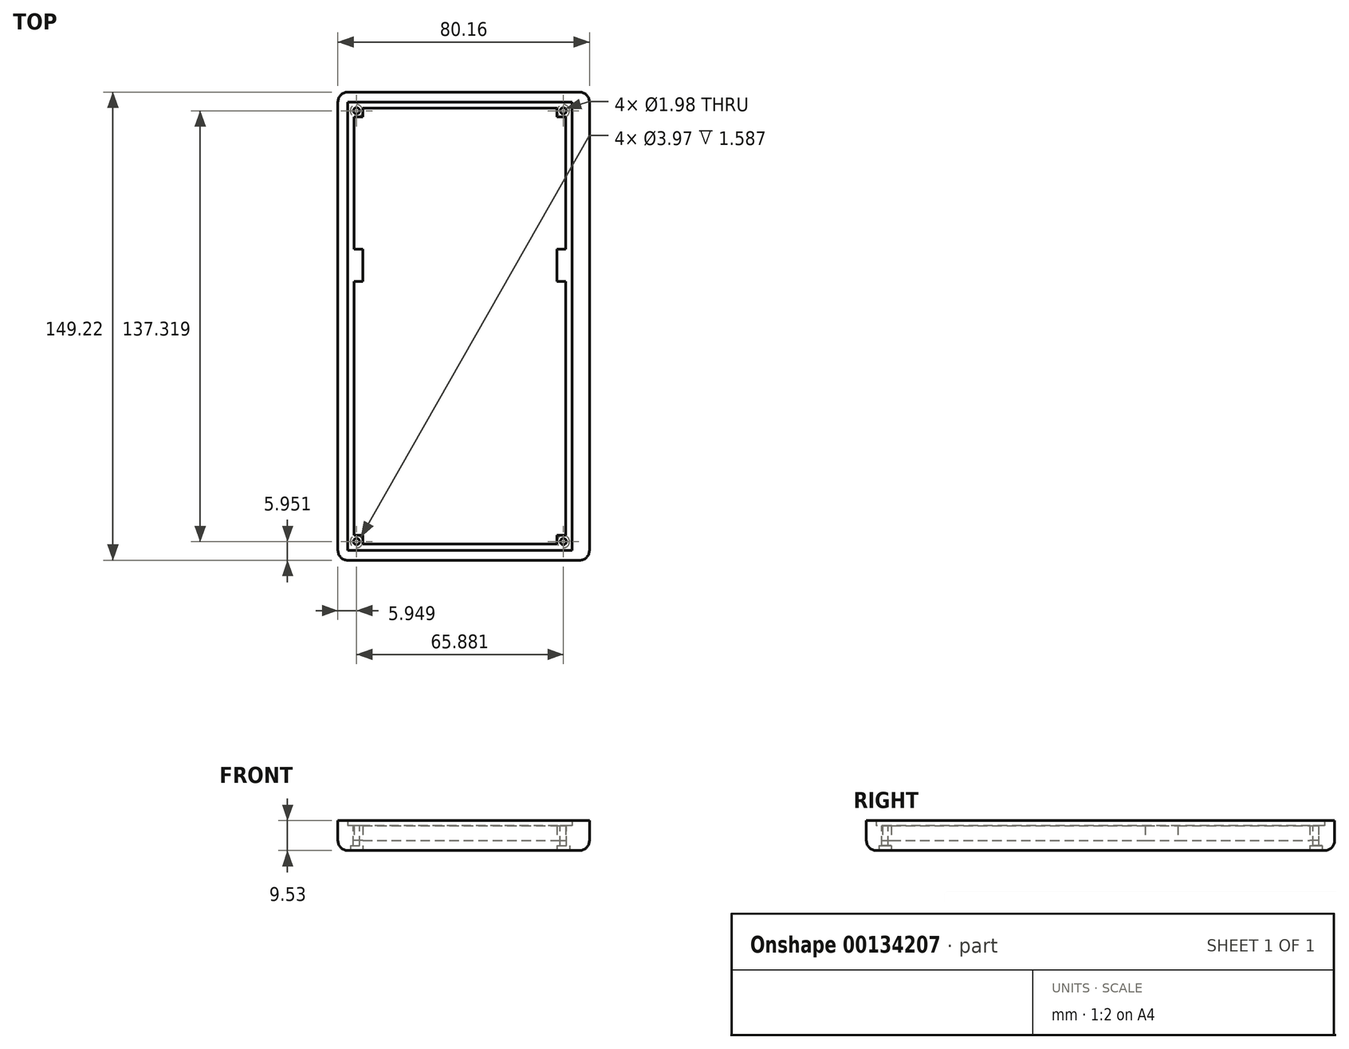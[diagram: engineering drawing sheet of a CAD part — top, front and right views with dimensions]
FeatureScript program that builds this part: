
annotation { "Feature Type Name" : "Feature", "Feature Type Description" : "" }
export const myFeature = defineFeature(function(context is Context, id is Id, definition is map)
    precondition{}
    {
        {
            var Q0;
            Q0=qCreatedBy(makeId("Top.planeOp"),FACE);
            var sketch = newSketch(context, id + "F0", { "sketchPlane" : qUnion([Q0])});
            skLineSegment(sketch, "E0.right", {"start": v(-36.9, -71.44) * mm, "end": v(-36.9, 71.44) * mm});
            skPoint(sketch, "E0.middle", {"position": v(0, 0) * mm});
            skLineSegment(sketch, "E1", {"start": v(-40.08, 0) * mm, "end": v(-40.08, -71.44) * mm});
            skLineSegment(sketch, "E2", {"start": v(-36.9, -74.61) * mm, "end": v(36.9, -74.61) * mm});
            skLineSegment(sketch, "E3", {"start": v(40.08, -71.44) * mm, "end": v(40.08, 71.44) * mm});
            skLineSegment(sketch, "E4", {"start": v(36.9, 74.61) * mm, "end": v(-36.9, 74.61) * mm});
            skLineSegment(sketch, "E5", {"start": v(-40.08, 71.44) * mm, "end": v(-40.08, 0) * mm});
            skPoint(sketch, "E6.visualSharp", {"position": v(-40.08, 74.61) * mm});
            skArc(sketch, "E6.filletArc", {"start": v(-36.9, 74.61) * mm, "mid": v(-39.15, 73.68) * mm, "end": v(-40.08, 71.44) * mm});
            skPoint(sketch, "E7.visualSharp", {"position": v(40.08, 74.61) * mm});
            skArc(sketch, "E7.filletArc", {"start": v(40.08, 71.44) * mm, "mid": v(39.15, 73.68) * mm, "end": v(36.9, 74.61) * mm});
            skPoint(sketch, "E8.visualSharp", {"position": v(40.08, -74.61) * mm});
            skArc(sketch, "E8.filletArc", {"start": v(36.9, -74.61) * mm, "mid": v(39.15, -73.68) * mm, "end": v(40.08, -71.44) * mm});
            skPoint(sketch, "E9.visualSharp", {"position": v(-40.08, -74.61) * mm});
            skArc(sketch, "E9.filletArc", {"start": v(-40.08, -71.44) * mm, "mid": v(-39.15, -73.68) * mm, "end": v(-36.9, -74.61) * mm});
            skLineSegment(sketch, "E10", {"start": v(34.53, 71.44) * mm, "end": v(34.53, -71.44) * mm});
            skLineSegment(sketch, "E11", {"start": v(-36.9, 71.44) * mm, "end": v(34.53, 71.44) * mm});
            skLineSegment(sketch, "E12", {"start": v(-36.9, -71.44) * mm, "end": v(34.53, -71.44) * mm});
            skSolve(sketch);
        }
        {
            var Q0;
            Q0=makeQuery(id+"F0.imprint","IMPRINT",FACE,{"disambiguationData":[TD([[makeQuery(id+"F0.imprint","IMPRINT",EDGE,{"derivedFrom":sQuery(id+"F0.wireOp",EDGE,"E0.right")}),1.0]])]});
            extrude(context, id + "F1", {"entities" : qUnion([Q0]), "depth" : 6.35 * mm});
        }
        {
            var Q0;
            Q0=makeQuery(id+"F1.opExtrude","CAP_FACE",FACE,{"disambiguationData":[OSD([sQuery(id+"F0.wireOp",EDGE,"E0.right"),sQuery(id+"F0.wireOp",EDGE,"E1"),sQuery(id+"F0.wireOp",EDGE,"E2"),sQuery(id+"F0.wireOp",EDGE,"E3"),sQuery(id+"F0.wireOp",EDGE,"E4"),sQuery(id+"F0.wireOp",EDGE,"E5"),sQuery(id+"F0.wireOp",EDGE,"E6.filletArc"),sQuery(id+"F0.wireOp",EDGE,"E7.filletArc"),sQuery(id+"F0.wireOp",EDGE,"E8.filletArc"),sQuery(id+"F0.wireOp",EDGE,"E9.filletArc"),sQuery(id+"F0.wireOp",EDGE,"E10"),sQuery(id+"F0.wireOp",EDGE,"E11"),sQuery(id+"F0.wireOp",EDGE,"E12")])],"isStart":true});
            var sketch = newSketch(context, id + "F2", { "sketchPlane" : qUnion([Q0])});
            skLineSegment(sketch, "E13.0", {"start": v(-40.08, -71.44) * mm, "end": v(-40.08, 71.44) * mm});
            skLineSegment(sketch, "E14.0", {"start": v(-36.9, 71.44) * mm, "end": v(-36.9, -71.44) * mm});
            skLineSegment(sketch, "E15.0", {"start": v(-36.9, 71.44) * mm, "end": v(34.53, 71.44) * mm});
            skLineSegment(sketch, "E16.0", {"start": v(34.53, -71.44) * mm, "end": v(34.53, 71.44) * mm});
            skLineSegment(sketch, "E17.0", {"start": v(-36.9, -71.44) * mm, "end": v(34.53, -71.44) * mm});
            skLineSegment(sketch, "E18.0.0", {"start": v(-40.08, 71.44) * mm, "end": v(-40.08, -71.44) * mm});
            skArc(sketch, "E18.0.1", {"start": v(-40.08, -71.44) * mm, "mid": v(-39.15, -73.68) * mm, "end": v(-36.9, -74.61) * mm});
            skLineSegment(sketch, "E18.0.2", {"start": v(-36.9, -74.61) * mm, "end": v(36.9, -74.61) * mm});
            skArc(sketch, "E18.0.3", {"start": v(36.9, -74.61) * mm, "mid": v(39.15, -73.68) * mm, "end": v(40.08, -71.44) * mm});
            skLineSegment(sketch, "E18.0.4", {"start": v(40.08, -71.44) * mm, "end": v(40.08, 71.44) * mm});
            skArc(sketch, "E18.0.5", {"start": v(40.08, 71.44) * mm, "mid": v(39.15, 73.68) * mm, "end": v(36.9, 74.61) * mm});
            skLineSegment(sketch, "E18.0.6", {"start": v(36.9, 74.61) * mm, "end": v(-36.9, 74.61) * mm});
            skArc(sketch, "E18.0.7", {"start": v(-36.9, 74.61) * mm, "mid": v(-39.15, 73.68) * mm, "end": v(-40.08, 71.44) * mm});
            skLineSegment(sketch, "E19.bottom", {"start": v(-32.15, 69.45) * mm, "end": v(29.77, 69.45) * mm});
            skLineSegment(sketch, "E19.top", {"start": v(-32.15, -69.45) * mm, "end": v(29.77, -69.45) * mm});
            skLineSegment(sketch, "E19.left", {"start": v(-34.92, 66.68) * mm, "end": v(-34.92, 24.6) * mm});
            skLineSegment(sketch, "E19.right", {"start": v(32.54, 66.68) * mm, "end": v(32.54, 24.6) * mm});
            skLineSegment(sketch, "E20", {"start": v(29.77, -69.45) * mm, "end": v(29.77, -66.67) * mm});
            skLineSegment(sketch, "E21", {"start": v(29.77, -66.67) * mm, "end": v(32.54, -66.67) * mm});
            skLineSegment(sketch, "E22", {"start": v(-34.92, -66.67) * mm, "end": v(-32.15, -66.67) * mm});
            skLineSegment(sketch, "E23", {"start": v(-32.15, -66.67) * mm, "end": v(-32.15, -69.45) * mm});
            skLineSegment(sketch, "E24.trimOffspring", {"start": v(32.54, 15.08) * mm, "end": v(32.54, -14.29) * mm});
            skLineSegment(sketch, "E25.trimOffspring", {"start": v(-34.92, 15.08) * mm, "end": v(-34.92, -14.29) * mm});
            skLineSegment(sketch, "E26", {"start": v(-34.92, 66.68) * mm, "end": v(32.54, 66.68) * mm});
            skLineSegment(sketch, "E27", {"start": v(-32.15, 69.45) * mm, "end": v(-32.15, 66.68) * mm});
            skLineSegment(sketch, "E28", {"start": v(29.77, 69.45) * mm, "end": v(29.77, 66.68) * mm});
            skLineSegment(sketch, "E29", {"start": v(-34.92, 24.6) * mm, "end": v(-34.92, 15.08) * mm});
            skLineSegment(sketch, "E30", {"start": v(32.54, 24.6) * mm, "end": v(32.54, 15.08) * mm});
            skLineSegment(sketch, "E31", {"start": v(-32.15, -19.84) * mm, "end": v(-32.15, -14.29) * mm});
            skLineSegment(sketch, "E32", {"start": v(-32.15, -14.29) * mm, "end": v(-34.93, -14.29) * mm});
            skLineSegment(sketch, "E33", {"start": v(-32.15, -19.84) * mm, "end": v(-32.15, -24.6) * mm});
            skLineSegment(sketch, "E34", {"start": v(-32.15, -24.6) * mm, "end": v(-34.92, -24.6) * mm});
            skLineSegment(sketch, "E35.bottom", {"start": v(32.54, -14.29) * mm, "end": v(29.77, -14.29) * mm});
            skLineSegment(sketch, "E35.top", {"start": v(32.54, -24.6) * mm, "end": v(29.77, -24.6) * mm});
            skLineSegment(sketch, "E35.right", {"start": v(29.77, -14.29) * mm, "end": v(29.77, -24.6) * mm});
            skLineSegment(sketch, "E36.trimOffspring", {"start": v(-34.92, -24.6) * mm, "end": v(-34.92, -66.67) * mm});
            skLineSegment(sketch, "E37.trimOffspring", {"start": v(32.54, -24.6) * mm, "end": v(32.54, -66.67) * mm});
            skLineSegment(sketch, "E38", {"start": v(-36.9, -19.84) * mm, "end": v(34.53, -19.84) * mm});
            skSolve(sketch);
        }
        {
            var Q0;
            Q0 = qSketchRegion(id + "F2", true);
            var Q1;
            Q1=makeQuery(id+"F2.imprint","IMPRINT",FACE,{"disambiguationData":[TD([[makeQuery(id+"F2.imprint","IMPRINT",EDGE,{"derivedFrom":sQuery(id+"F2.wireOp",EDGE,"E14.0")}),1.0]])]});
            var Q2;
            {var subQ5=sQuery(id+"F2.wireOp",EDGE,"E15.0");Q2=makeQuery(id+"F2.imprint","IMPRINT",FACE,{"disambiguationData":[TD([[makeQuery(id+"F2.imprint","IMPRINT",EDGE,{"derivedFrom":subQ5}),-1.0]])]});}
            extrude(context, id + "F3", {"entities" : qUnion([Q0, Q1, Q2]), "operationType" : NewBodyOperationType.ADD, "oppositeDirection" : true, "depth" : 4.76 * mm});
        }
        {
            var Q0;
            Q0=makeQuery(id+"F3.boolean.opBoolean","MERGE",FACE,{"derivedFrom":[makeQuery(id+"F1.opExtrude","CAP_FACE",FACE,{"disambiguationData":[OSD([sQuery(id+"F0.wireOp",EDGE,"E0.right"),sQuery(id+"F0.wireOp",EDGE,"E1"),sQuery(id+"F0.wireOp",EDGE,"E2"),sQuery(id+"F0.wireOp",EDGE,"E3"),sQuery(id+"F0.wireOp",EDGE,"E4"),sQuery(id+"F0.wireOp",EDGE,"E5"),sQuery(id+"F0.wireOp",EDGE,"E6.filletArc"),sQuery(id+"F0.wireOp",EDGE,"E7.filletArc"),sQuery(id+"F0.wireOp",EDGE,"E8.filletArc"),sQuery(id+"F0.wireOp",EDGE,"E9.filletArc"),sQuery(id+"F0.wireOp",EDGE,"E10"),sQuery(id+"F0.wireOp",EDGE,"E11"),sQuery(id+"F0.wireOp",EDGE,"E12")])],"isStart":true}),makeQuery(id+"F3.opExtrude","CAP_FACE",FACE,{"disambiguationData":[OSD([sQuery(id+"F2.wireOp",EDGE,"E18.0.0"),sQuery(id+"F2.wireOp",EDGE,"E18.0.1"),sQuery(id+"F2.wireOp",EDGE,"E18.0.2"),sQuery(id+"F2.wireOp",EDGE,"E18.0.3"),sQuery(id+"F2.wireOp",EDGE,"E18.0.4"),sQuery(id+"F2.wireOp",EDGE,"E18.0.5"),sQuery(id+"F2.wireOp",EDGE,"E18.0.6"),sQuery(id+"F2.wireOp",EDGE,"E18.0.7"),sQuery(id+"F2.wireOp",EDGE,"E19.bottom"),sQuery(id+"F2.wireOp",EDGE,"E19.top"),sQuery(id+"F2.wireOp",EDGE,"E19.left"),sQuery(id+"F2.wireOp",EDGE,"E19.right"),sQuery(id+"F2.wireOp",EDGE,"E20"),sQuery(id+"F2.wireOp",EDGE,"E21"),sQuery(id+"F2.wireOp",EDGE,"E22"),sQuery(id+"F2.wireOp",EDGE,"E23"),sQuery(id+"F2.wireOp",EDGE,"E24.trimOffspring"),sQuery(id+"F2.wireOp",EDGE,"E25.trimOffspring"),sQuery(id+"F2.wireOp",EDGE,"E26"),sQuery(id+"F2.wireOp",EDGE,"E27"),sQuery(id+"F2.wireOp",EDGE,"E28"),sQuery(id+"F2.wireOp",EDGE,"E29"),sQuery(id+"F2.wireOp",EDGE,"E30"),sQuery(id+"F2.wireOp",EDGE,"E31"),sQuery(id+"F2.wireOp",EDGE,"E32"),sQuery(id+"F2.wireOp",EDGE,"E33"),sQuery(id+"F2.wireOp",EDGE,"E34"),sQuery(id+"F2.wireOp",EDGE,"E35.bottom"),sQuery(id+"F2.wireOp",EDGE,"E35.top"),sQuery(id+"F2.wireOp",EDGE,"E35.right"),sQuery(id+"F2.wireOp",EDGE,"E36.trimOffspring"),sQuery(id+"F2.wireOp",EDGE,"E37.trimOffspring")])],"isStart":true})]});
            var sketch = newSketch(context, id + "F4", { "sketchPlane" : qUnion([Q0])});
            skLineSegment(sketch, "E39.0.0", {"start": v(-40.08, 71.44) * mm, "end": v(-40.08, -71.44) * mm});
            skArc(sketch, "E39.0.1", {"start": v(-40.08, -71.44) * mm, "mid": v(-39.15, -73.68) * mm, "end": v(-36.9, -74.61) * mm});
            skLineSegment(sketch, "E39.0.2", {"start": v(-36.9, -74.61) * mm, "end": v(36.9, -74.61) * mm});
            skArc(sketch, "E39.0.3", {"start": v(36.9, -74.61) * mm, "mid": v(39.15, -73.68) * mm, "end": v(40.08, -71.44) * mm});
            skLineSegment(sketch, "E39.0.4", {"start": v(40.08, -71.44) * mm, "end": v(40.08, 71.44) * mm});
            skArc(sketch, "E39.0.5", {"start": v(40.08, 71.44) * mm, "mid": v(39.15, 73.68) * mm, "end": v(36.9, 74.61) * mm});
            skLineSegment(sketch, "E39.0.6", {"start": v(36.9, 74.61) * mm, "end": v(-36.9, 74.61) * mm});
            skArc(sketch, "E39.0.7", {"start": v(-36.9, 74.61) * mm, "mid": v(-39.15, 73.68) * mm, "end": v(-40.08, 71.44) * mm});
            skSolve(sketch);
        }
        {
            var Q0;
            Q0=makeQuery(id+"F4.imprint","IMPRINT",FACE,{"disambiguationData":[TD([[makeQuery(id+"F4.imprint","IMPRINT",EDGE,{"derivedFrom":makeQuery(id+"F3.opExtrude","CAP_EDGE",EDGE,{"disambiguationData":[OSD([sQuery(id+"F2.wireOp",EDGE,"E19.bottom")])],"isStart":true})}),-1.0]])]});
            var Q1;
            Q1=makeQuery(id+"F4.imprint","IMPRINT",FACE,{"disambiguationData":[TD([[makeQuery(id+"F4.imprint","IMPRINT",EDGE,{"derivedFrom":sQuery(id+"F4.wireOp",EDGE,"E39.0.0")}),-1.0]])]});
            extrude(context, id + "F5", {"entities" : qUnion([Q0, Q1]), "operationType" : NewBodyOperationType.ADD, "depth" : 3.17 * mm});
        }
        {
            var Q0;
            Q0=makeQuery(id+"F5.opExtrude","CAP_EDGE",EDGE,{"disambiguationData":[OSD([sQuery(id+"F4.wireOp",EDGE,"E39.0.0")])],"isStart":false});
            fillet(context, id + "F6", {"entities" : qUnion([Q0]), "radius" : 3.17 * mm, "tangentPropagation" : true, "allowEdgeOverflow" : false});
        }
        {
            var Q0;
            Q0=makeQuery(id+"F3.opExtrude","CAP_FACE",FACE,{"disambiguationData":[OSD([sQuery(id+"F2.wireOp",EDGE,"E18.0.0"),sQuery(id+"F2.wireOp",EDGE,"E18.0.1"),sQuery(id+"F2.wireOp",EDGE,"E18.0.2"),sQuery(id+"F2.wireOp",EDGE,"E18.0.3"),sQuery(id+"F2.wireOp",EDGE,"E18.0.4"),sQuery(id+"F2.wireOp",EDGE,"E18.0.5"),sQuery(id+"F2.wireOp",EDGE,"E18.0.6"),sQuery(id+"F2.wireOp",EDGE,"E18.0.7"),sQuery(id+"F2.wireOp",EDGE,"E19.bottom"),sQuery(id+"F2.wireOp",EDGE,"E19.top"),sQuery(id+"F2.wireOp",EDGE,"E19.left"),sQuery(id+"F2.wireOp",EDGE,"E19.right"),sQuery(id+"F2.wireOp",EDGE,"E20"),sQuery(id+"F2.wireOp",EDGE,"E21"),sQuery(id+"F2.wireOp",EDGE,"E22"),sQuery(id+"F2.wireOp",EDGE,"E23"),sQuery(id+"F2.wireOp",EDGE,"E24.trimOffspring"),sQuery(id+"F2.wireOp",EDGE,"E25.trimOffspring"),sQuery(id+"F2.wireOp",EDGE,"E26"),sQuery(id+"F2.wireOp",EDGE,"E27"),sQuery(id+"F2.wireOp",EDGE,"E28"),sQuery(id+"F2.wireOp",EDGE,"E29"),sQuery(id+"F2.wireOp",EDGE,"E30"),sQuery(id+"F2.wireOp",EDGE,"E31"),sQuery(id+"F2.wireOp",EDGE,"E32"),sQuery(id+"F2.wireOp",EDGE,"E33"),sQuery(id+"F2.wireOp",EDGE,"E34"),sQuery(id+"F2.wireOp",EDGE,"E35.bottom"),sQuery(id+"F2.wireOp",EDGE,"E35.top"),sQuery(id+"F2.wireOp",EDGE,"E35.right"),sQuery(id+"F2.wireOp",EDGE,"E36.trimOffspring"),sQuery(id+"F2.wireOp",EDGE,"E37.trimOffspring")])],"isStart":false});
            var sketch = newSketch(context, id + "F7", { "sketchPlane" : qUnion([Q0])});
            skLineSegment(sketch, "E40.0.0", {"start": v(-36.9, -71.44) * mm, "end": v(34.53, -71.44) * mm});
            skLineSegment(sketch, "E40.0.1", {"start": v(34.53, -71.44) * mm, "end": v(34.53, 71.44) * mm});
            skLineSegment(sketch, "E40.0.2", {"start": v(34.53, 71.44) * mm, "end": v(-36.9, 71.44) * mm});
            skLineSegment(sketch, "E40.0.3", {"start": v(-36.9, 71.44) * mm, "end": v(-36.9, -71.44) * mm});
            skLineSegment(sketch, "E41.0.0", {"start": v(-40.08, 71.44) * mm, "end": v(-40.08, -71.44) * mm});
            skArc(sketch, "E41.0.1", {"start": v(-40.08, -71.44) * mm, "mid": v(-39.15, -73.68) * mm, "end": v(-36.9, -74.61) * mm});
            skLineSegment(sketch, "E41.0.2", {"start": v(-36.9, -74.61) * mm, "end": v(36.9, -74.61) * mm});
            skArc(sketch, "E41.0.3", {"start": v(36.9, -74.61) * mm, "mid": v(39.15, -73.68) * mm, "end": v(40.08, -71.44) * mm});
            skLineSegment(sketch, "E41.0.4", {"start": v(40.08, -71.44) * mm, "end": v(40.08, 71.44) * mm});
            skArc(sketch, "E41.0.5", {"start": v(40.08, 71.44) * mm, "mid": v(39.15, 73.68) * mm, "end": v(36.9, 74.61) * mm});
            skLineSegment(sketch, "E41.0.6", {"start": v(36.9, 74.61) * mm, "end": v(-36.9, 74.61) * mm});
            skArc(sketch, "E41.0.7", {"start": v(-36.9, 74.61) * mm, "mid": v(-39.15, 73.68) * mm, "end": v(-40.08, 71.44) * mm});
            skLineSegment(sketch, "E42.top", {"start": v(-32.15, -71.44) * mm, "end": v(-36.9, -71.44) * mm});
            skLineSegment(sketch, "E43", {"start": v(-36.12, -71.44) * mm, "end": v(-36.12, -70.64) * mm});
            skLineSegment(sketch, "E44", {"start": v(-36.12, -70.64) * mm, "end": v(-36.9, -70.64) * mm});
            skLineSegment(sketch, "E45.bottom", {"start": v(-32.15, -66.68) * mm, "end": v(-36.12, -66.68) * mm});
            skLineSegment(sketch, "E45.top", {"start": v(-32.15, -70.64) * mm, "end": v(-36.12, -70.64) * mm});
            skLineSegment(sketch, "E45.left", {"start": v(-32.15, -66.68) * mm, "end": v(-32.15, -70.64) * mm});
            skLineSegment(sketch, "E45.right", {"start": v(-36.12, -66.68) * mm, "end": v(-36.12, -70.64) * mm});
            skLineSegment(sketch, "E46", {"start": v(-36.12, -66.68) * mm, "end": v(-32.15, -70.64) * mm});
            skLineSegment(sketch, "E47", {"start": v(-32.15, -66.68) * mm, "end": v(-36.12, -70.64) * mm});
            skCircle(sketch, "E48", {"center": v(-34.13, -68.66) * mm, "radius": 1 * mm});
            skCircle(sketch, "E49", {"center": v(31.75, -68.66) * mm, "radius": 1 * mm});
            skPoint(sketch, "E50.centerSnap0", {"position": v(-33.54, -66.68) * mm});
            skLineSegment(sketch, "E51", {"start": v(-34.13, -68.66) * mm, "end": v(-34.13, 22.45) * mm});
            skCircle(sketch, "E52", {"center": v(-34.13, 16.27) * mm, "radius": 1 * mm});
            skLineSegment(sketch, "E53", {"start": v(-34.13, 16.27) * mm, "end": v(38.66, 16.27) * mm});
            skCircle(sketch, "E54", {"center": v(31.75, 16.27) * mm, "radius": 1 * mm});
            skLineSegment(sketch, "E55.bottom", {"start": v(-36.9, 71.44) * mm, "end": v(-36.12, 71.44) * mm});
            skLineSegment(sketch, "E55.top", {"start": v(-36.9, 70.64) * mm, "end": v(-36.12, 70.64) * mm});
            skLineSegment(sketch, "E55.left", {"start": v(-36.9, 71.44) * mm, "end": v(-36.9, 70.64) * mm});
            skLineSegment(sketch, "E55.right", {"start": v(-36.12, 71.44) * mm, "end": v(-36.12, 70.64) * mm});
            skLineSegment(sketch, "E56.bottom", {"start": v(-36.12, 70.64) * mm, "end": v(-32.15, 70.64) * mm});
            skLineSegment(sketch, "E56.top", {"start": v(-36.12, 66.67) * mm, "end": v(-32.15, 66.67) * mm});
            skLineSegment(sketch, "E56.left", {"start": v(-36.12, 70.64) * mm, "end": v(-36.12, 66.67) * mm});
            skLineSegment(sketch, "E56.right", {"start": v(-32.15, 70.64) * mm, "end": v(-32.15, 66.67) * mm});
            skLineSegment(sketch, "E57", {"start": v(-36.12, 66.67) * mm, "end": v(-32.15, 70.64) * mm});
            skLineSegment(sketch, "E58", {"start": v(-36.12, 70.64) * mm, "end": v(-32.15, 66.67) * mm});
            skCircle(sketch, "E59", {"center": v(-34.13, 68.66) * mm, "radius": 1 * mm});
            skLineSegment(sketch, "E60", {"start": v(-34.13, 68.66) * mm, "end": v(39.27, 68.66) * mm});
            skCircle(sketch, "E61", {"center": v(31.75, 68.66) * mm, "radius": 1 * mm});
            skCircle(sketch, "E62", {"center": v(-34.13, 22.62) * mm, "radius": 1 * mm});
            skCircle(sketch, "E63", {"center": v(31.75, 22.62) * mm, "radius": 1 * mm});
            skSolve(sketch);
        }
        {
            var Q0;
            Q0=sQuery(id+"F7.wireOp",VERTEX,"E51.start");
            var Q1;
            Q1=sQuery(id+"F7.wireOp",VERTEX,"E49.center");
            var Q2;
            Q2=sQuery(id+"F7.wireOp",VERTEX,"E61.center");
            var Q3;
            Q3=sQuery(id+"F7.wireOp",VERTEX,"E60.start");
            var Q4;
            Q4=makeQuery(id+"F1.opExtrude","SWEPT_BODY",BODY,{"disambiguationData":[OSD([sQuery(id+"F0.wireOp",EDGE,"E0.right"),sQuery(id+"F0.wireOp",EDGE,"E1"),sQuery(id+"F0.wireOp",EDGE,"E2"),sQuery(id+"F0.wireOp",EDGE,"E3"),sQuery(id+"F0.wireOp",EDGE,"E4"),sQuery(id+"F0.wireOp",EDGE,"E5"),sQuery(id+"F0.wireOp",EDGE,"E6.filletArc"),sQuery(id+"F0.wireOp",EDGE,"E7.filletArc"),sQuery(id+"F0.wireOp",EDGE,"E8.filletArc"),sQuery(id+"F0.wireOp",EDGE,"E9.filletArc"),sQuery(id+"F0.wireOp",EDGE,"E10"),sQuery(id+"F0.wireOp",EDGE,"E11"),sQuery(id+"F0.wireOp",EDGE,"E12")])]});
            hole(context, id + "F8", {"style" : HoleStyle.SIMPLE, "endStyle" : HoleEndStyle.THROUGH, "holeDiameter" : 1.98 * mm, "locations" : qUnion([Q0, Q1, Q2, Q3]), "scope" : qUnion([Q4]), "isTappedThrough" : true});
        }
        {
            var Q0;
            Q0=makeQuery(id+"F5.opExtrude","CAP_FACE",FACE,{"disambiguationData":[OSD([sQuery(id+"F4.wireOp",EDGE,"E39.0.0"),sQuery(id+"F4.wireOp",EDGE,"E39.0.1"),sQuery(id+"F4.wireOp",EDGE,"E39.0.2"),sQuery(id+"F4.wireOp",EDGE,"E39.0.3"),sQuery(id+"F4.wireOp",EDGE,"E39.0.4"),sQuery(id+"F4.wireOp",EDGE,"E39.0.5"),sQuery(id+"F4.wireOp",EDGE,"E39.0.6"),sQuery(id+"F4.wireOp",EDGE,"E39.0.7")])],"isStart":false});
            var sketch = newSketch(context, id + "F9", { "sketchPlane" : qUnion([Q0])});
            skLineSegment(sketch, "E64.0.0", {"start": v(-36.9, -71.44) * mm, "end": v(36.9, -71.44) * mm});
            skLineSegment(sketch, "E64.0.1", {"start": v(36.9, -71.44) * mm, "end": v(36.9, 71.44) * mm});
            skLineSegment(sketch, "E64.0.2", {"start": v(36.9, 71.44) * mm, "end": v(-36.9, 71.44) * mm});
            skLineSegment(sketch, "E64.0.3", {"start": v(-36.9, 71.44) * mm, "end": v(-36.9, -71.44) * mm});
            skCircle(sketch, "E65", {"center": v(-34.13, 68.66) * mm, "radius": 1.98 * mm});
            skCircle(sketch, "E66", {"center": v(31.75, 68.66) * mm, "radius": 1.98 * mm});
            skCircle(sketch, "E67", {"center": v(31.75, -68.66) * mm, "radius": 1.98 * mm});
            skCircle(sketch, "E68", {"center": v(-34.13, -68.66) * mm, "radius": 1.98 * mm});
            skSolve(sketch);
        }
        {
            var Q0;
            Q0=makeQuery(id+"F9.imprint","IMPRINT",FACE,{"disambiguationData":[TD([[makeQuery(id+"F9.imprint","IMPRINT",EDGE,{"derivedFrom":sQuery(id+"F9.wireOp",EDGE,"E65")}),1.0]])]});
            var Q1;
            Q1=makeQuery(id+"F9.imprint","IMPRINT",FACE,{"disambiguationData":[TD([[makeQuery(id+"F9.imprint","IMPRINT",EDGE,{"derivedFrom":sQuery(id+"F9.wireOp",EDGE,"E66")}),1.0]])]});
            var Q2;
            Q2=makeQuery(id+"F9.imprint","IMPRINT",FACE,{"disambiguationData":[TD([[makeQuery(id+"F9.imprint","IMPRINT",EDGE,{"derivedFrom":sQuery(id+"F9.wireOp",EDGE,"E68")}),1.0]])]});
            var Q3;
            Q3=makeQuery(id+"F9.imprint","IMPRINT",FACE,{"disambiguationData":[TD([[makeQuery(id+"F9.imprint","IMPRINT",EDGE,{"derivedFrom":sQuery(id+"F9.wireOp",EDGE,"E67")}),1.0]])]});
            extrude(context, id + "F10", {"entities" : qUnion([Q0, Q1, Q2, Q3]), "operationType" : NewBodyOperationType.REMOVE, "oppositeDirection" : true, "depth" : 1.59 * mm});
        }
    });
